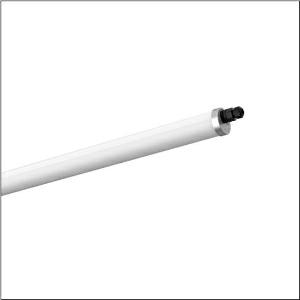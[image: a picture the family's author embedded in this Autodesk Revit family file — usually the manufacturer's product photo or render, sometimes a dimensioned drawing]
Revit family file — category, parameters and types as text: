
# Revit family: monsun_r__31_tube_51ft10dn480a_9fe9
name_source: partatom
category: Lighting Fixtures
units: mm (PartAtom-declared; Revit-internal decimal feet)

## family parameters
Cut with Voids When Loaded = No
Host = Face
Light Source = No
Part Type = Normal
Room Calculation Point = No
Round Connector Dimension = Use Diameter
Shared = No

## types (1)
- Monsun® 31 Tube (1 x LED, 8000 lm, 50 W, 4000K)
    Apparent Load = 50 VA
    CIE Flux Codes = 42 71 89 91 100
    Color Rendering = 80
    Color Temperature = 4000K
    Default Elevation = 1800 mm
    Description = Monsun® 31 Tube, tubular luminaire, primary optical cover: diffuser, of PMMA, light emission: direct distribution, primary light characteristic: symmetric, installation type: suspended mounting, surface-mounted, LED, rated luminous flux: 8.000lm, luminous efficacy: 160lm/W, light colour: 840, colour temperature: 4000K, with with 1 terminal, 5-pole, max. 2.5mm², through-wiring: 5x 1.5mm², mains connection: 220..240V, AC, 50/60Hz, rated input power: 50W, housing, cylindrical, of PMMA, semi-transparent, matt white, with luminaire and ceiling fastening, V4A, mounting with brackets of stainless steel, length: 1.570mm, diameter: 75mm, end cap, of stainless steel (V4A), protection rating (complete): IP67/IP69K, insulation class (complete): insulation class I (protective earthing), certification: CE, UKCA, impact resistance: IK07, permissible operating ambient temperature: -20..+40°C, corresponds to IFS (International Featured Standards) requirements for safety and quality in the food industry, usage in unprotected outdoor area possible with horizontal mounting, contact your sales advisor before using the luminaires in applications with unclear chemical exposure, large temperature fluctuations or condensation-forming humidity, packaging unit: 1 piece
    Height = 83 mm
    Lamp = 1 x LED
    Lamp Light Flux = 8000 lm
    Lamp Power = 50 W
    Lamp count = 1
    Length = 1570 mm
    Luminous efficacy = 160 lm/W
    Manufacturer = Siteco
    ModVariant = No
    Model = 51FT10DN480A
    Mounting Place = Ceiling
    Mounting Type = Pendant
    Number of Poles = 1
    OnlyDefault = Yes
    Power Factor = 1
    Product Name = Monsun® 31 Tube
    Product group = tubular luminaire
    ProductGroupID = 906
    Protection Class = Protection class I
    RLX_Detail_Level = 1
    RLX_Emergency_Light_Flux = 0 lm
    RLX_Emergency_Type = 0
    RLX_Emergency_Type_DB = No
    RlxData = <blob elided: 25409 chars, md5=96597295>
    Socket = socket
    Standby Power = 0 W
    System Light Flux = 8000 lm
    System Power = 50 W
    Type Comments = Product without accessories
    Type Image = l_1228461.jpg
    URL = http://relux.com
    VarID = ---
    Voltage = 0 V
    Weight = 0.00 kg
    Width = 75 mm

## geometry (parser evidence)
native form markers: Blend x4, Sweep x13
no freeform markers — native parametric forms only
